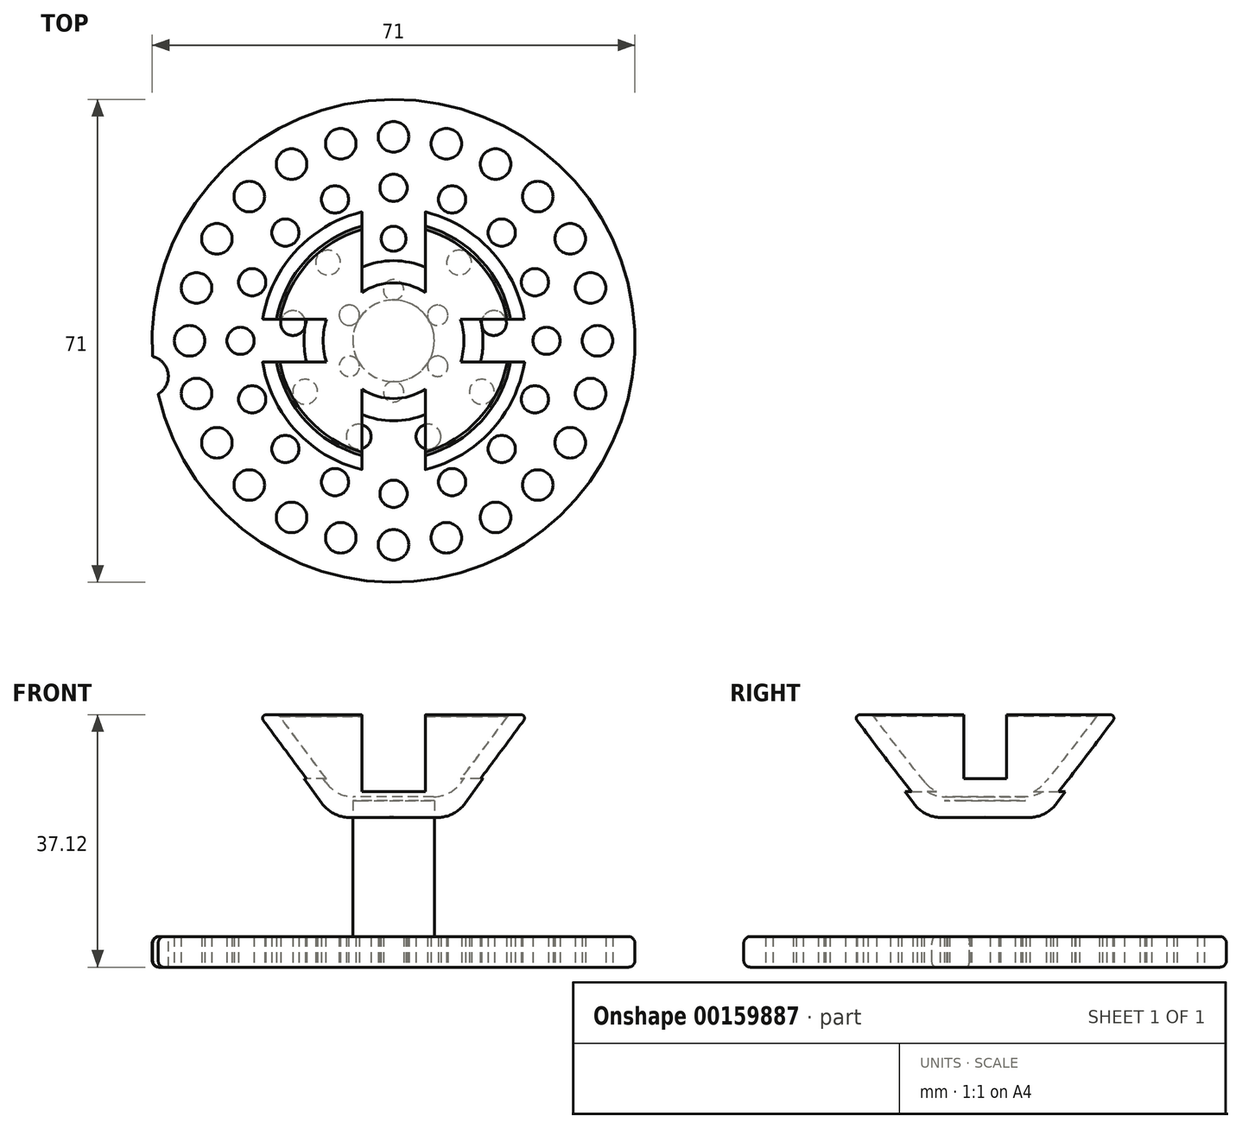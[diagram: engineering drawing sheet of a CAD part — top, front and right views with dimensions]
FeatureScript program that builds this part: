
annotation { "Feature Type Name" : "Feature", "Feature Type Description" : "" }
export const myFeature = defineFeature(function(context is Context, id is Id, definition is map)
    precondition{}
    {
        {
            var Q0;
            Q0=qCreatedBy(makeId("Top.planeOp"),FACE);
            var sketch = newSketch(context, id + "F0", { "sketchPlane" : qUnion([Q0])});
            skCircle(sketch, "E0", {"center": v(0, 0) * mm, "radius": 35.5 * mm});
            skSolve(sketch);
        }
        {
            var Q0;
            Q0=makeQuery(id+"F0.imprint","IMPRINT",FACE,{"disambiguationData":[TD([[makeQuery(id+"F0.imprint","IMPRINT",EDGE,{"derivedFrom":sQuery(id+"F0.wireOp",EDGE,"E0")}),1.0]])]});
            var sketch = newSketch(context, id + "F1", { "sketchPlane" : qUnion([Q0])});
            skCircle(sketch, "E1", {"center": v(0, 0) * mm, "radius": 7.5 * mm, "construction": true});
            skCircle(sketch, "E2", {"center": v(0, 7.5) * mm, "radius": 1.5 * mm});
            skCircle(sketch, "E3.1.1", {"center": v(-6.5, 3.75) * mm, "radius": 1.5 * mm});
            skCircle(sketch, "E3.2.1", {"center": v(-6.5, -3.75) * mm, "radius": 1.5 * mm});
            skCircle(sketch, "E3.3.1", {"center": v(0, -7.5) * mm, "radius": 1.5 * mm});
            skCircle(sketch, "E3.4.1", {"center": v(6.5, -3.75) * mm, "radius": 1.5 * mm});
            skCircle(sketch, "E3.5.1", {"center": v(6.5, 3.75) * mm, "radius": 1.5 * mm});
            skSolve(sketch);
        }
        {
            var Q0;
            Q0=makeQuery(id+"F0.imprint","IMPRINT",FACE,{"disambiguationData":[TD([[makeQuery(id+"F0.imprint","IMPRINT",EDGE,{"derivedFrom":sQuery(id+"F0.wireOp",EDGE,"E0")}),1.0]])]});
            var sketch = newSketch(context, id + "F2", { "sketchPlane" : qUnion([Q0])});
            skCircle(sketch, "E4", {"center": v(0, 0) * mm, "radius": 15 * mm, "construction": true});
            skCircle(sketch, "E5", {"center": v(0, 15) * mm, "radius": 1.83 * mm});
            skCircle(sketch, "E6.1.0", {"center": v(-9.64, 11.5) * mm, "radius": 1.83 * mm});
            skCircle(sketch, "E6.2.0", {"center": v(-14.77, 2.6) * mm, "radius": 1.83 * mm});
            skCircle(sketch, "E6.3.0", {"center": v(-13, -7.5) * mm, "radius": 1.83 * mm});
            skCircle(sketch, "E6.4.0", {"center": v(-5.13, -14.1) * mm, "radius": 1.83 * mm});
            skCircle(sketch, "E6.5.0", {"center": v(5.13, -14.1) * mm, "radius": 1.83 * mm});
            skCircle(sketch, "E6.6.0", {"center": v(13, -7.5) * mm, "radius": 1.83 * mm});
            skCircle(sketch, "E6.7.0", {"center": v(14.77, 2.6) * mm, "radius": 1.83 * mm});
            skCircle(sketch, "E6.8.0", {"center": v(9.64, 11.5) * mm, "radius": 1.83 * mm});
            skSolve(sketch);
        }
        {
            var Q0;
            Q0=makeQuery(id+"F0.imprint","IMPRINT",FACE,{"disambiguationData":[TD([[makeQuery(id+"F0.imprint","IMPRINT",EDGE,{"derivedFrom":sQuery(id+"F0.wireOp",EDGE,"E0")}),1.0]])]});
            var sketch = newSketch(context, id + "F3", { "sketchPlane" : qUnion([Q0])});
            skCircle(sketch, "E7", {"center": v(0, 0) * mm, "radius": 22.5 * mm, "construction": true});
            skCircle(sketch, "E8", {"center": v(0, 22.5) * mm, "radius": 2 * mm});
            skCircle(sketch, "E9.1.0", {"center": v(-8.61, 20.79) * mm, "radius": 2 * mm});
            skCircle(sketch, "E9.2.0", {"center": v(-15.9, 15.9) * mm, "radius": 2 * mm});
            skCircle(sketch, "E9.3.0", {"center": v(-20.79, 8.61) * mm, "radius": 2 * mm});
            skCircle(sketch, "E9.4.0", {"center": v(-22.5, 0) * mm, "radius": 2 * mm});
            skCircle(sketch, "E9.5.0", {"center": v(-20.79, -8.61) * mm, "radius": 2 * mm});
            skCircle(sketch, "E9.6.0", {"center": v(-15.9, -15.9) * mm, "radius": 2 * mm});
            skCircle(sketch, "E9.7.0", {"center": v(-8.61, -20.79) * mm, "radius": 2 * mm});
            skCircle(sketch, "E9.8.0", {"center": v(0, -22.5) * mm, "radius": 2 * mm});
            skCircle(sketch, "E9.9.0", {"center": v(8.61, -20.79) * mm, "radius": 2 * mm});
            skCircle(sketch, "E9.10.0", {"center": v(15.9, -15.9) * mm, "radius": 2 * mm});
            skCircle(sketch, "E9.11.0", {"center": v(20.79, -8.61) * mm, "radius": 2 * mm});
            skCircle(sketch, "E9.12.0", {"center": v(22.5, 0) * mm, "radius": 2 * mm});
            skCircle(sketch, "E9.13.0", {"center": v(20.79, 8.61) * mm, "radius": 2 * mm});
            skCircle(sketch, "E9.14.0", {"center": v(15.9, 15.9) * mm, "radius": 2 * mm});
            skCircle(sketch, "E9.15.0", {"center": v(8.61, 20.79) * mm, "radius": 2 * mm});
            skSolve(sketch);
        }
        {
            var Q0;
            Q0=makeQuery(id+"F0.imprint","IMPRINT",FACE,{"disambiguationData":[TD([[makeQuery(id+"F0.imprint","IMPRINT",EDGE,{"derivedFrom":sQuery(id+"F0.wireOp",EDGE,"E0")}),1.0]])]});
            var sketch = newSketch(context, id + "F4", { "sketchPlane" : qUnion([Q0])});
            skCircle(sketch, "E10", {"center": v(0, 0) * mm, "radius": 30 * mm, "construction": true});
            skCircle(sketch, "E11", {"center": v(0, 30) * mm, "radius": 2.25 * mm});
            skCircle(sketch, "E12.1.0", {"center": v(-7.76, 28.98) * mm, "radius": 2.25 * mm});
            skCircle(sketch, "E12.2.0", {"center": v(-15, 25.98) * mm, "radius": 2.25 * mm});
            skCircle(sketch, "E13.1.3.0", {"center": v(-21.21, 21.21) * mm, "radius": 2.25 * mm});
            skCircle(sketch, "E13.1.4.0", {"center": v(-25.98, 15) * mm, "radius": 2.25 * mm});
            skCircle(sketch, "E13.1.5.0", {"center": v(-28.98, 7.76) * mm, "radius": 2.25 * mm});
            skCircle(sketch, "E13.1.6.0", {"center": v(-30, 0) * mm, "radius": 2.25 * mm});
            skCircle(sketch, "E13.1.7.0", {"center": v(-28.98, -7.76) * mm, "radius": 2.25 * mm});
            skCircle(sketch, "E13.1.8.0", {"center": v(-25.98, -15) * mm, "radius": 2.25 * mm});
            skCircle(sketch, "E13.1.9.0", {"center": v(-21.21, -21.21) * mm, "radius": 2.25 * mm});
            skCircle(sketch, "E13.1.10.0", {"center": v(-15, -25.98) * mm, "radius": 2.25 * mm});
            skCircle(sketch, "E13.1.11.0", {"center": v(-7.76, -28.98) * mm, "radius": 2.25 * mm});
            skCircle(sketch, "E13.1.12.0", {"center": v(0, -30) * mm, "radius": 2.25 * mm});
            skCircle(sketch, "E13.1.13.0", {"center": v(7.76, -28.98) * mm, "radius": 2.25 * mm});
            skCircle(sketch, "E13.1.14.0", {"center": v(15, -25.98) * mm, "radius": 2.25 * mm});
            skCircle(sketch, "E13.1.15.0", {"center": v(21.21, -21.21) * mm, "radius": 2.25 * mm});
            skCircle(sketch, "E13.1.16.0", {"center": v(25.98, -15) * mm, "radius": 2.25 * mm});
            skCircle(sketch, "E13.1.17.0", {"center": v(28.98, -7.76) * mm, "radius": 2.25 * mm});
            skCircle(sketch, "E13.1.18.0", {"center": v(30, 0) * mm, "radius": 2.25 * mm});
            skCircle(sketch, "E13.1.19.0", {"center": v(28.98, 7.76) * mm, "radius": 2.25 * mm});
            skCircle(sketch, "E13.1.20.0", {"center": v(25.98, 15) * mm, "radius": 2.25 * mm});
            skCircle(sketch, "E13.1.21.0", {"center": v(21.21, 21.21) * mm, "radius": 2.25 * mm});
            skCircle(sketch, "E13.1.22.0", {"center": v(15, 25.98) * mm, "radius": 2.25 * mm});
            skCircle(sketch, "E13.1.23.0", {"center": v(7.76, 28.98) * mm, "radius": 2.25 * mm});
            skSolve(sketch);
        }
        {
            var Q0;
            Q0=qSketchRegion(id+"F4",true);
            extrude(context, id + "F5", {"entities" : qUnion([Q0]), "depth" : 5 * mm});
        }
        {
            var Q0;
            Q0=qSketchRegion(id+"F3",true);
            extrude(context, id + "F6", {"entities" : qUnion([Q0]), "depth" : 5 * mm});
        }
        {
            var Q0;
            Q0=qSketchRegion(id+"F2",true);
            extrude(context, id + "F7", {"entities" : qUnion([Q0]), "depth" : 5 * mm});
        }
        {
            var Q0;
            Q0=qSketchRegion(id+"F1",true);
            extrude(context, id + "F8", {"entities" : qUnion([Q0]), "depth" : 5 * mm});
        }
        {
            var Q0;
            Q0=qSketchRegion(id+"F0",true);
            extrude(context, id + "F9", {"entities" : qUnion([Q0]), "depth" : 4.5 * mm});
        }
        {
            var Q0;
            Q0=makeQuery(id+"F5.opExtrude","SWEPT_BODY",BODY,{"disambiguationData":[OSD([sQuery(id+"F4.wireOp",EDGE,"E11")])]});
            var Q1;
            Q1=makeQuery(id+"F5.opExtrude","SWEPT_BODY",BODY,{"disambiguationData":[OSD([sQuery(id+"F4.wireOp",EDGE,"E13.1.3.0")])]});
            var Q2;
            Q2=makeQuery(id+"F5.opExtrude","SWEPT_BODY",BODY,{"disambiguationData":[OSD([sQuery(id+"F4.wireOp",EDGE,"E13.1.7.0")])]});
            var Q3;
            Q3=makeQuery(id+"F5.opExtrude","SWEPT_BODY",BODY,{"disambiguationData":[OSD([sQuery(id+"F4.wireOp",EDGE,"E12.1.0")])]});
            var Q4;
            Q4=makeQuery(id+"F5.opExtrude","SWEPT_BODY",BODY,{"disambiguationData":[OSD([sQuery(id+"F4.wireOp",EDGE,"E12.2.0")])]});
            var Q5;
            Q5=makeQuery(id+"F5.opExtrude","SWEPT_BODY",BODY,{"disambiguationData":[OSD([sQuery(id+"F4.wireOp",EDGE,"E13.1.4.0")])]});
            var Q6;
            Q6=makeQuery(id+"F5.opExtrude","SWEPT_BODY",BODY,{"disambiguationData":[OSD([sQuery(id+"F4.wireOp",EDGE,"E13.1.5.0")])]});
            var Q7;
            Q7=makeQuery(id+"F5.opExtrude","SWEPT_BODY",BODY,{"disambiguationData":[OSD([sQuery(id+"F4.wireOp",EDGE,"E13.1.6.0")])]});
            var Q8;
            Q8=makeQuery(id+"F5.opExtrude","SWEPT_BODY",BODY,{"disambiguationData":[OSD([sQuery(id+"F4.wireOp",EDGE,"E13.1.8.0")])]});
            var Q9;
            Q9=makeQuery(id+"F5.opExtrude","SWEPT_BODY",BODY,{"disambiguationData":[OSD([sQuery(id+"F4.wireOp",EDGE,"E13.1.9.0")])]});
            var Q10;
            Q10=makeQuery(id+"F5.opExtrude","SWEPT_BODY",BODY,{"disambiguationData":[OSD([sQuery(id+"F4.wireOp",EDGE,"E13.1.10.0")])]});
            var Q11;
            Q11=makeQuery(id+"F5.opExtrude","SWEPT_BODY",BODY,{"disambiguationData":[OSD([sQuery(id+"F4.wireOp",EDGE,"E13.1.11.0")])]});
            var Q12;
            Q12=makeQuery(id+"F5.opExtrude","SWEPT_BODY",BODY,{"disambiguationData":[OSD([sQuery(id+"F4.wireOp",EDGE,"E13.1.12.0")])]});
            var Q13;
            Q13=makeQuery(id+"F5.opExtrude","SWEPT_BODY",BODY,{"disambiguationData":[OSD([sQuery(id+"F4.wireOp",EDGE,"E13.1.13.0")])]});
            var Q14;
            Q14=makeQuery(id+"F5.opExtrude","SWEPT_BODY",BODY,{"disambiguationData":[OSD([sQuery(id+"F4.wireOp",EDGE,"E13.1.14.0")])]});
            var Q15;
            Q15=makeQuery(id+"F5.opExtrude","SWEPT_BODY",BODY,{"disambiguationData":[OSD([sQuery(id+"F4.wireOp",EDGE,"E13.1.15.0")])]});
            var Q16;
            Q16=makeQuery(id+"F5.opExtrude","SWEPT_BODY",BODY,{"disambiguationData":[OSD([sQuery(id+"F4.wireOp",EDGE,"E13.1.16.0")])]});
            var Q17;
            Q17=makeQuery(id+"F5.opExtrude","SWEPT_BODY",BODY,{"disambiguationData":[OSD([sQuery(id+"F4.wireOp",EDGE,"E13.1.17.0")])]});
            var Q18;
            Q18=makeQuery(id+"F5.opExtrude","SWEPT_BODY",BODY,{"disambiguationData":[OSD([sQuery(id+"F4.wireOp",EDGE,"E13.1.18.0")])]});
            var Q19;
            Q19=makeQuery(id+"F5.opExtrude","SWEPT_BODY",BODY,{"disambiguationData":[OSD([sQuery(id+"F4.wireOp",EDGE,"E13.1.19.0")])]});
            var Q20;
            Q20=makeQuery(id+"F5.opExtrude","SWEPT_BODY",BODY,{"disambiguationData":[OSD([sQuery(id+"F4.wireOp",EDGE,"E13.1.20.0")])]});
            var Q21;
            Q21=makeQuery(id+"F5.opExtrude","SWEPT_BODY",BODY,{"disambiguationData":[OSD([sQuery(id+"F4.wireOp",EDGE,"E13.1.21.0")])]});
            var Q22;
            Q22=makeQuery(id+"F5.opExtrude","SWEPT_BODY",BODY,{"disambiguationData":[OSD([sQuery(id+"F4.wireOp",EDGE,"E13.1.22.0")])]});
            var Q23;
            Q23=makeQuery(id+"F5.opExtrude","SWEPT_BODY",BODY,{"disambiguationData":[OSD([sQuery(id+"F4.wireOp",EDGE,"E13.1.23.0")])]});
            var Q24;
            Q24=makeQuery(id+"F6.opExtrude","SWEPT_BODY",BODY,{"disambiguationData":[OSD([sQuery(id+"F3.wireOp",EDGE,"E9.15.0")])]});
            var Q25;
            Q25=makeQuery(id+"F6.opExtrude","SWEPT_BODY",BODY,{"disambiguationData":[OSD([sQuery(id+"F3.wireOp",EDGE,"E8")])]});
            var Q26;
            Q26=makeQuery(id+"F6.opExtrude","SWEPT_BODY",BODY,{"disambiguationData":[OSD([sQuery(id+"F3.wireOp",EDGE,"E9.1.0")])]});
            var Q27;
            Q27=makeQuery(id+"F6.opExtrude","SWEPT_BODY",BODY,{"disambiguationData":[OSD([sQuery(id+"F3.wireOp",EDGE,"E9.2.0")])]});
            var Q28;
            Q28=makeQuery(id+"F6.opExtrude","SWEPT_BODY",BODY,{"disambiguationData":[OSD([sQuery(id+"F3.wireOp",EDGE,"E9.3.0")])]});
            var Q29;
            Q29=makeQuery(id+"F6.opExtrude","SWEPT_BODY",BODY,{"disambiguationData":[OSD([sQuery(id+"F3.wireOp",EDGE,"E9.4.0")])]});
            var Q30;
            Q30=makeQuery(id+"F6.opExtrude","SWEPT_BODY",BODY,{"disambiguationData":[OSD([sQuery(id+"F3.wireOp",EDGE,"E9.5.0")])]});
            var Q31;
            Q31=makeQuery(id+"F6.opExtrude","SWEPT_BODY",BODY,{"disambiguationData":[OSD([sQuery(id+"F3.wireOp",EDGE,"E9.6.0")])]});
            var Q32;
            Q32=makeQuery(id+"F6.opExtrude","SWEPT_BODY",BODY,{"disambiguationData":[OSD([sQuery(id+"F3.wireOp",EDGE,"E9.7.0")])]});
            var Q33;
            Q33=makeQuery(id+"F6.opExtrude","SWEPT_BODY",BODY,{"disambiguationData":[OSD([sQuery(id+"F3.wireOp",EDGE,"E9.8.0")])]});
            var Q34;
            Q34=makeQuery(id+"F6.opExtrude","SWEPT_BODY",BODY,{"disambiguationData":[OSD([sQuery(id+"F3.wireOp",EDGE,"E9.9.0")])]});
            var Q35;
            Q35=makeQuery(id+"F6.opExtrude","SWEPT_BODY",BODY,{"disambiguationData":[OSD([sQuery(id+"F3.wireOp",EDGE,"E9.10.0")])]});
            var Q36;
            Q36=makeQuery(id+"F6.opExtrude","SWEPT_BODY",BODY,{"disambiguationData":[OSD([sQuery(id+"F3.wireOp",EDGE,"E9.11.0")])]});
            var Q37;
            Q37=makeQuery(id+"F6.opExtrude","SWEPT_BODY",BODY,{"disambiguationData":[OSD([sQuery(id+"F3.wireOp",EDGE,"E9.12.0")])]});
            var Q38;
            Q38=makeQuery(id+"F6.opExtrude","SWEPT_BODY",BODY,{"disambiguationData":[OSD([sQuery(id+"F3.wireOp",EDGE,"E9.13.0")])]});
            var Q39;
            Q39=makeQuery(id+"F6.opExtrude","SWEPT_BODY",BODY,{"disambiguationData":[OSD([sQuery(id+"F3.wireOp",EDGE,"E9.14.0")])]});
            var Q40;
            Q40=makeQuery(id+"F7.opExtrude","SWEPT_BODY",BODY,{"disambiguationData":[OSD([sQuery(id+"F2.wireOp",EDGE,"E6.8.0")])]});
            var Q41;
            Q41=makeQuery(id+"F7.opExtrude","SWEPT_BODY",BODY,{"disambiguationData":[OSD([sQuery(id+"F2.wireOp",EDGE,"E6.7.0")])]});
            var Q42;
            Q42=makeQuery(id+"F7.opExtrude","SWEPT_BODY",BODY,{"disambiguationData":[OSD([sQuery(id+"F2.wireOp",EDGE,"E6.6.0")])]});
            var Q43;
            Q43=makeQuery(id+"F7.opExtrude","SWEPT_BODY",BODY,{"disambiguationData":[OSD([sQuery(id+"F2.wireOp",EDGE,"E6.5.0")])]});
            var Q44;
            Q44=makeQuery(id+"F7.opExtrude","SWEPT_BODY",BODY,{"disambiguationData":[OSD([sQuery(id+"F2.wireOp",EDGE,"E6.4.0")])]});
            var Q45;
            Q45=makeQuery(id+"F7.opExtrude","SWEPT_BODY",BODY,{"disambiguationData":[OSD([sQuery(id+"F2.wireOp",EDGE,"E6.3.0")])]});
            var Q46;
            Q46=makeQuery(id+"F7.opExtrude","SWEPT_BODY",BODY,{"disambiguationData":[OSD([sQuery(id+"F2.wireOp",EDGE,"E6.2.0")])]});
            var Q47;
            Q47=makeQuery(id+"F7.opExtrude","SWEPT_BODY",BODY,{"disambiguationData":[OSD([sQuery(id+"F2.wireOp",EDGE,"E6.1.0")])]});
            var Q48;
            Q48=makeQuery(id+"F7.opExtrude","SWEPT_BODY",BODY,{"disambiguationData":[OSD([sQuery(id+"F2.wireOp",EDGE,"E5")])]});
            var Q49;
            Q49=makeQuery(id+"F8.opExtrude","SWEPT_BODY",BODY,{"disambiguationData":[OSD([sQuery(id+"F1.wireOp",EDGE,"E2")])]});
            var Q50;
            Q50=makeQuery(id+"F8.opExtrude","SWEPT_BODY",BODY,{"disambiguationData":[OSD([sQuery(id+"F1.wireOp",EDGE,"E3.5.1")])]});
            var Q51;
            Q51=makeQuery(id+"F8.opExtrude","SWEPT_BODY",BODY,{"disambiguationData":[OSD([sQuery(id+"F1.wireOp",EDGE,"E3.4.1")])]});
            var Q52;
            Q52=makeQuery(id+"F8.opExtrude","SWEPT_BODY",BODY,{"disambiguationData":[OSD([sQuery(id+"F1.wireOp",EDGE,"E3.3.1")])]});
            var Q53;
            Q53=makeQuery(id+"F8.opExtrude","SWEPT_BODY",BODY,{"disambiguationData":[OSD([sQuery(id+"F1.wireOp",EDGE,"E3.2.1")])]});
            var Q54;
            Q54=makeQuery(id+"F8.opExtrude","SWEPT_BODY",BODY,{"disambiguationData":[OSD([sQuery(id+"F1.wireOp",EDGE,"E3.1.1")])]});
            var Q55;
            Q55=makeQuery(id+"F9.opExtrude","SWEPT_BODY",BODY,{"disambiguationData":[OSD([sQuery(id+"F0.wireOp",EDGE,"E0")])]});
            booleanBodies(context, id + "F10", {"operationType" : BooleanOperationType.SUBTRACTION, "tools" : qUnion([Q0, Q1, Q2, Q3, Q4, Q5, Q6, Q7, Q8, Q9, Q10, Q11, Q12, Q13, Q14, Q15, Q16, Q17, Q18, Q19, Q20, Q21, Q22, Q23, Q24, Q25, Q26, Q27, Q28, Q29, Q30, Q31, Q32, Q33, Q34, Q35, Q36, Q37, Q38, Q39, Q40, Q41, Q42, Q43, Q44, Q45, Q46, Q47, Q48, Q49, Q50, Q51, Q52, Q53, Q54]), "targets" : qUnion([Q55])});
        }
        {
            var Q0;
            Q0=makeQuery(id+"F9.opExtrude","CAP_EDGE",EDGE,{"disambiguationData":[OSD([sQuery(id+"F0.wireOp",EDGE,"E0")])],"isStart":true});
            var Q1;
            Q1=makeQuery(id+"F9.opExtrude","CAP_EDGE",EDGE,{"disambiguationData":[OSD([sQuery(id+"F0.wireOp",EDGE,"E0")])],"isStart":false});
            fillet(context, id + "F11", {"entities" : qUnion([Q0, Q1]), "radius" : 1 * mm, "tangentPropagation" : true, "allowEdgeOverflow" : false});
        }
        {
            var Q0;
            Q0=makeQuery(id+"F9.opExtrude","CAP_FACE",FACE,{"disambiguationData":[OSD([sQuery(id+"F0.wireOp",EDGE,"E0")])],"isStart":false});
            var sketch = newSketch(context, id + "F12", { "sketchPlane" : qUnion([Q0])});
            skCircle(sketch, "E14", {"center": v(0, 0) * mm, "radius": 6 * mm});
            skSolve(sketch);
        }
        {
            var Q0;
            Q0=makeQuery(id+"F12.imprint","IMPRINT",FACE,{"disambiguationData":[TD([[makeQuery(id+"F12.imprint","IMPRINT",EDGE,{"derivedFrom":sQuery(id+"F12.wireOp",EDGE,"E14")}),1.0]])]});
            extrude(context, id + "F13", {"entities" : qUnion([Q0]), "operationType" : NewBodyOperationType.ADD, "depth" : 20 * mm, "offsetDistance" : 25 * mm});
        }
        {
            var Q0;
            Q0=makeQuery(id+"F9.opExtrude","CAP_FACE",FACE,{"disambiguationData":[OSD([sQuery(id+"F0.wireOp",EDGE,"E0")])],"isStart":false});
            var sketch = newSketch(context, id + "F14", { "sketchPlane" : qUnion([Q0])});
            skCircle(sketch, "E15", {"center": v(0, 0) * mm, "radius": 36.5 * mm, "construction": true});
            skCircle(sketch, "E16", {"center": v(-36.12, -5.23) * mm, "radius": 3 * mm});
            skSolve(sketch);
        }
        {
            var Q0;
            Q0=makeQuery(id+"F14.imprint","IMPRINT",FACE,{"disambiguationData":[TD([[makeQuery(id+"F14.imprint","IMPRINT",EDGE,{"derivedFrom":sQuery(id+"F14.wireOp",EDGE,"E16")}),1.0]])]});
            extrude(context, id + "F15", {"entities" : qUnion([Q0]), "operationType" : NewBodyOperationType.REMOVE, "oppositeDirection" : true, "depth" : 25 * mm});
        }
        {
            var Q0;
            Q0=qCreatedBy(makeId("Front.planeOp"),FACE);
            var sketch = newSketch(context, id + "F16", { "sketchPlane" : qUnion([Q0])});
            skLineSegment(sketch, "E17", {"start": v(0, 64.6) * mm, "end": v(0, 86.12) * mm, "construction": true});
            skLineSegment(sketch, "E18", {"start": v(-20, 85.12) * mm, "end": v(-9, 69.99) * mm});
            skLineSegment(sketch, "E19", {"start": v(0, 70.12) * mm, "end": v(0, 86.12) * mm});
            skLineSegment(sketch, "E20", {"start": v(-20, 85.12) * mm, "end": v(-17.2, 85.12) * mm});
            skLineSegment(sketch, "E21", {"start": v(-17.2, 85.12) * mm, "end": v(-8.44, 73.07) * mm});
            skLineSegment(sketch, "E22", {"start": v(-8.44, 73.07) * mm, "end": v(0, 73.07) * mm});
            skLineSegment(sketch, "E23", {"start": v(-9, 69.99) * mm, "end": v(0, 70.12) * mm});
            skSolve(sketch);
        }
        {
            var Q0;
            Q0=makeQuery(id+"F16.imprint","IMPRINT",FACE,{"disambiguationData":[TD([[makeQuery(id+"F16.imprint","IMPRINT",EDGE,{"derivedFrom":sQuery(id+"F16.wireOp",EDGE,"E18")}),1.0]])]});
            var Q1;
            Q1=sQuery(id+"F16.wireOp",EDGE,"E19");
            revolve(context, id + "F17", {"operationType" : NewBodyOperationType.ADD, "surfaceOperationType" : NewSurfaceOperationType.NEW, "entities" : qUnion([Q0]), "axis" : qUnion([Q1]), "revolveType" : RevolveType.FULL});
        }
        {
            var Q0;
            Q0=makeQuery(id+"F17.opRevolve","SWEPT_BODY",BODY,{"disambiguationData":[OSD([sQuery(id+"F16.wireOp",EDGE,"E18"),sQuery(id+"F16.wireOp",EDGE,"ekqP7qBP-ulQC-kSXt-n5Og-ePe3p9eNB1yX"),sQuery(id+"F16.wireOp",EDGE,"E19"),sQuery(id+"F16.wireOp",EDGE,"E20"),sQuery(id+"F16.wireOp",EDGE,"E21"),sQuery(id+"F16.wireOp",EDGE,"E22")])]});
            transform(context, id + "F18", {"entities" : qUnion([Q0]), "transformType" : TransformType.TRANSLATION_3D, "dx" : 0 * mm, "dy" : 0 * mm, "dz" : -48 * mm, "makeCopy" : false});
        }
        {
            var Q0;
            Q0=qCreatedBy(makeId("Front.planeOp"),FACE);
            var sketch = newSketch(context, id + "F19", { "sketchPlane" : qUnion([Q0])});
            skLineSegment(sketch, "E24.bottom", {"start": v(4.66, 25.8) * mm, "end": v(-4.66, 25.8) * mm});
            skLineSegment(sketch, "E24.top", {"start": v(4.66, 51.49) * mm, "end": v(-4.66, 51.49) * mm});
            skLineSegment(sketch, "E24.left", {"start": v(4.66, 25.8) * mm, "end": v(4.66, 51.49) * mm});
            skLineSegment(sketch, "E24.right", {"start": v(-4.66, 25.8) * mm, "end": v(-4.66, 51.49) * mm});
            skPoint(sketch, "E24.middle", {"position": v(0, 38.65) * mm});
            skLineSegment(sketch, "E25", {"start": v(0, 59.77) * mm, "end": v(0, 0) * mm, "construction": true});
            skSolve(sketch);
        }
        {
            var Q0;
            Q0 = qSketchRegion(id + "F19", true);
            extrude(context, id + "F20", {"entities" : qUnion([Q0]), "endBound" : BoundingType.SYMMETRIC, "depth" : 45 * mm, "offsetDistance" : 25 * mm});
        }
        {
            var Q0;
            {var subQ0=sQuery(id+"F16.wireOp",EDGE,"E20");var subQ1=sQuery(id+"F16.wireOp",EDGE,"E21");Q0=makeQuery(id+"F24O2oq0PfPqQpG_3.opBoolean","SPLIT",EDGE,{"disambiguationData":[TD([makeQuery(id+"FJ4bphDz8gUAr4i_3.opPattern","COPY",FACE,{"derivedFrom":makeQuery(id+"F20.opExtrude","SWEPT_FACE",FACE,{"disambiguationData":[OSD([sQuery(id+"F19.wireOp",EDGE,"E24.left")])]}),"instanceName":"2"})])],"derivedFrom":makeQuery(id+"F17.opRevolve","SWEPT_EDGE",EDGE,{"disambiguationData":[OSD([subQ0,subQ1])]})});}
            var Q1;
            {var subQ0=sQuery(id+"F16.wireOp",EDGE,"E20");var subQ1=sQuery(id+"F16.wireOp",EDGE,"E21");Q1=makeQuery(id+"F24O2oq0PfPqQpG_3.opBoolean","SPLIT",EDGE,{"disambiguationData":[TD([makeQuery(id+"FJ4bphDz8gUAr4i_3.opPattern","COPY",FACE,{"derivedFrom":makeQuery(id+"F20.opExtrude","SWEPT_FACE",FACE,{"disambiguationData":[OSD([sQuery(id+"F19.wireOp",EDGE,"E24.left")])]}),"instanceName":"1"})])],"derivedFrom":makeQuery(id+"F17.opRevolve","SWEPT_EDGE",EDGE,{"disambiguationData":[OSD([subQ0,subQ1])]})});}
            var Q2;
            {var subQ0=sQuery(id+"F16.wireOp",EDGE,"E20");var subQ1=sQuery(id+"F16.wireOp",EDGE,"E21");Q2=makeQuery(id+"F24O2oq0PfPqQpG_3.opBoolean","SPLIT",EDGE,{"disambiguationData":[TD([makeQuery(id+"F20.opExtrude","SWEPT_FACE",FACE,{"disambiguationData":[OSD([sQuery(id+"F19.wireOp",EDGE,"E24.left")])]})])],"derivedFrom":makeQuery(id+"F17.opRevolve","SWEPT_EDGE",EDGE,{"disambiguationData":[OSD([subQ0,subQ1])]})});}
            var Q3;
            {var subQ0=sQuery(id+"F16.wireOp",EDGE,"E20");var subQ1=sQuery(id+"F16.wireOp",EDGE,"E21");Q3=makeQuery(id+"F24O2oq0PfPqQpG_3.opBoolean","SPLIT",EDGE,{"disambiguationData":[TD([makeQuery(id+"F20.opExtrude","SWEPT_FACE",FACE,{"disambiguationData":[OSD([sQuery(id+"F19.wireOp",EDGE,"E24.right")])]})])],"derivedFrom":makeQuery(id+"F17.opRevolve","SWEPT_EDGE",EDGE,{"disambiguationData":[OSD([subQ0,subQ1])]})});}
            var Q4;
            {var subQ0=sQuery(id+"F16.wireOp",EDGE,"E20");var subQ1=sQuery(id+"F16.wireOp",EDGE,"E21");Q4=makeQuery(id+"F24O2oq0PfPqQpG_3.opBoolean","SPLIT",EDGE,{"disambiguationData":[TD([makeQuery(id+"FJ4bphDz8gUAr4i_3.opPattern","COPY",FACE,{"derivedFrom":makeQuery(id+"F20.opExtrude","SWEPT_FACE",FACE,{"disambiguationData":[OSD([sQuery(id+"F19.wireOp",EDGE,"E24.left")])]}),"instanceName":"4"})])],"derivedFrom":makeQuery(id+"F17.opRevolve","SWEPT_EDGE",EDGE,{"disambiguationData":[OSD([subQ0,subQ1])]})});}
            var Q5;
            {var subQ0=sQuery(id+"F16.wireOp",EDGE,"E20");var subQ1=sQuery(id+"F16.wireOp",EDGE,"E21");Q5=makeQuery(id+"F24O2oq0PfPqQpG_3.opBoolean","SPLIT",EDGE,{"disambiguationData":[TD([makeQuery(id+"FJ4bphDz8gUAr4i_3.opPattern","COPY",FACE,{"derivedFrom":makeQuery(id+"F20.opExtrude","SWEPT_FACE",FACE,{"disambiguationData":[OSD([sQuery(id+"F19.wireOp",EDGE,"E24.left")])]}),"instanceName":"3"})])],"derivedFrom":makeQuery(id+"F17.opRevolve","SWEPT_EDGE",EDGE,{"disambiguationData":[OSD([subQ0,subQ1])]})});}
            chamfer(context, id + "F21", {"entities" : qUnion([Q0, Q1, Q2, Q3, Q4, Q5]), "width" : 0.6 * mm, "tangentPropagation" : true});
        }
        {
            var Q0;
            {var subQ0=sQuery(id+"F16.wireOp",EDGE,"E18");var subQ1=sQuery(id+"F16.wireOp",EDGE,"E20");Q0=makeQuery(id+"F24O2oq0PfPqQpG_3.opBoolean","SPLIT",EDGE,{"disambiguationData":[TD([makeQuery(id+"FJ4bphDz8gUAr4i_3.opPattern","COPY",FACE,{"derivedFrom":makeQuery(id+"F20.opExtrude","SWEPT_FACE",FACE,{"disambiguationData":[OSD([sQuery(id+"F19.wireOp",EDGE,"E24.left")])]}),"instanceName":"2"})])],"derivedFrom":makeQuery(id+"F17.opRevolve","SWEPT_EDGE",EDGE,{"disambiguationData":[OSD([subQ0,subQ1])]})});}
            var Q1;
            {var subQ0=sQuery(id+"F16.wireOp",EDGE,"E18");var subQ1=sQuery(id+"F16.wireOp",EDGE,"E20");Q1=makeQuery(id+"F24O2oq0PfPqQpG_3.opBoolean","SPLIT",EDGE,{"disambiguationData":[TD([makeQuery(id+"FJ4bphDz8gUAr4i_3.opPattern","COPY",FACE,{"derivedFrom":makeQuery(id+"F20.opExtrude","SWEPT_FACE",FACE,{"disambiguationData":[OSD([sQuery(id+"F19.wireOp",EDGE,"E24.left")])]}),"instanceName":"1"})])],"derivedFrom":makeQuery(id+"F17.opRevolve","SWEPT_EDGE",EDGE,{"disambiguationData":[OSD([subQ0,subQ1])]})});}
            var Q2;
            {var subQ0=sQuery(id+"F16.wireOp",EDGE,"E18");var subQ1=sQuery(id+"F16.wireOp",EDGE,"E20");Q2=makeQuery(id+"F24O2oq0PfPqQpG_3.opBoolean","SPLIT",EDGE,{"disambiguationData":[TD([makeQuery(id+"F20.opExtrude","SWEPT_FACE",FACE,{"disambiguationData":[OSD([sQuery(id+"F19.wireOp",EDGE,"E24.left")])]})])],"derivedFrom":makeQuery(id+"F17.opRevolve","SWEPT_EDGE",EDGE,{"disambiguationData":[OSD([subQ0,subQ1])]})});}
            var Q3;
            {var subQ0=sQuery(id+"F16.wireOp",EDGE,"E18");var subQ1=sQuery(id+"F16.wireOp",EDGE,"E20");Q3=makeQuery(id+"F24O2oq0PfPqQpG_3.opBoolean","SPLIT",EDGE,{"disambiguationData":[TD([makeQuery(id+"F20.opExtrude","SWEPT_FACE",FACE,{"disambiguationData":[OSD([sQuery(id+"F19.wireOp",EDGE,"E24.right")])]})])],"derivedFrom":makeQuery(id+"F17.opRevolve","SWEPT_EDGE",EDGE,{"disambiguationData":[OSD([subQ0,subQ1])]})});}
            var Q4;
            {var subQ0=sQuery(id+"F16.wireOp",EDGE,"E18");var subQ1=sQuery(id+"F16.wireOp",EDGE,"E20");Q4=makeQuery(id+"F24O2oq0PfPqQpG_3.opBoolean","SPLIT",EDGE,{"disambiguationData":[TD([makeQuery(id+"FJ4bphDz8gUAr4i_3.opPattern","COPY",FACE,{"derivedFrom":makeQuery(id+"F20.opExtrude","SWEPT_FACE",FACE,{"disambiguationData":[OSD([sQuery(id+"F19.wireOp",EDGE,"E24.left")])]}),"instanceName":"4"})])],"derivedFrom":makeQuery(id+"F17.opRevolve","SWEPT_EDGE",EDGE,{"disambiguationData":[OSD([subQ0,subQ1])]})});}
            var Q5;
            {var subQ0=sQuery(id+"F16.wireOp",EDGE,"E18");var subQ1=sQuery(id+"F16.wireOp",EDGE,"E20");Q5=makeQuery(id+"F24O2oq0PfPqQpG_3.opBoolean","SPLIT",EDGE,{"disambiguationData":[TD([makeQuery(id+"FJ4bphDz8gUAr4i_3.opPattern","COPY",FACE,{"derivedFrom":makeQuery(id+"F20.opExtrude","SWEPT_FACE",FACE,{"disambiguationData":[OSD([sQuery(id+"F19.wireOp",EDGE,"E24.left")])]}),"instanceName":"3"})])],"derivedFrom":makeQuery(id+"F17.opRevolve","SWEPT_EDGE",EDGE,{"disambiguationData":[OSD([subQ0,subQ1])]})});}
            fillet(context, id + "F22", {"entities" : qUnion([Q0, Q1, Q2, Q3, Q4, Q5]), "tangentPropagation" : true, "radius" : .5 * mm, "defaultsChanged" : false, "vertexSettings" : [], "allowEdgeOverflow" : false});
        }
        {
            var Q0;
            Q0=makeQuery(id+"F17.opRevolve","SWEPT_EDGE",EDGE,{"disambiguationData":[OSD([sQuery(id+"F16.wireOp",EDGE,"E18"),sQuery(id+"F16.wireOp",EDGE,"E23")])]});
            fillet(context, id + "F23", {"entities" : qUnion([Q0]), "tangentPropagation" : true, "radius" : 5 * mm, "defaultsChanged" : false, "vertexSettings" : [], "allowEdgeOverflow" : false});
        }
        {
            var Q0;
            Q0=makeQuery(id+"F17.opRevolve","SWEPT_EDGE",EDGE,{"disambiguationData":[OSD([sQuery(id+"F16.wireOp",EDGE,"E21"),sQuery(id+"F16.wireOp",EDGE,"E22")])]});
            fillet(context, id + "F24", {"entities" : qUnion([Q0]), "tangentPropagation" : true, "radius" : 5 * mm, "defaultsChanged" : false, "vertexSettings" : [], "allowEdgeOverflow" : false});
        }
        {
            var Q0;
            Q0=qCreatedBy(makeId("Right.planeOp"),FACE);
            var sketch = newSketch(context, id + "F25", { "sketchPlane" : qUnion([Q0])});
            skLineSegment(sketch, "E26.bottom", {"start": v(3.19, 41.64) * mm, "end": v(-3.12, 41.64) * mm});
            skLineSegment(sketch, "E26.top", {"start": v(3.19, 24.31) * mm, "end": v(-3.12, 24.31) * mm});
            skLineSegment(sketch, "E26.left", {"start": v(3.19, 41.64) * mm, "end": v(3.19, 24.31) * mm});
            skLineSegment(sketch, "E26.right", {"start": v(-3.12, 41.64) * mm, "end": v(-3.12, 24.31) * mm});
            skSolve(sketch);
        }
        {
            var Q0;
            Q0 = qSketchRegion(id + "F25", true);
            extrude(context, id + "F26", {"entities" : qUnion([Q0]), "endBound" : BoundingType.SYMMETRIC, "depth" : 45 * mm, "offsetDistance" : 25 * mm});
        }
        {
            var Q0;
            Q0=makeQuery(id+"F26.opExtrude","SWEPT_BODY",BODY,{"disambiguationData":[OSD([sQuery(id+"F25.wireOp",EDGE,"E26.bottom"),sQuery(id+"F25.wireOp",EDGE,"E26.top"),sQuery(id+"F25.wireOp",EDGE,"E26.left"),sQuery(id+"F25.wireOp",EDGE,"E26.right")])]});
            transform(context, id + "F27", {"entities" : qUnion([Q0]), "transformType" : TransformType.TRANSLATION_3D, "dx" : 0 * mm, "dy" : 0 * mm, "dz" : 3.4 * mm, "makeCopy" : false});
        }
        {
            var Q0;
            Q0=makeQuery(id+"F20.opExtrude","SWEPT_BODY",BODY,{"disambiguationData":[OSD([sQuery(id+"F19.wireOp",EDGE,"E24.bottom"),sQuery(id+"F19.wireOp",EDGE,"E24.top"),sQuery(id+"F19.wireOp",EDGE,"E24.left"),sQuery(id+"F19.wireOp",EDGE,"E24.right")])]});
            var Q1;
            Q1=makeQuery(id+"F26.opExtrude","SWEPT_BODY",BODY,{"disambiguationData":[OSD([sQuery(id+"F25.wireOp",EDGE,"E26.bottom"),sQuery(id+"F25.wireOp",EDGE,"E26.top"),sQuery(id+"F25.wireOp",EDGE,"E26.left"),sQuery(id+"F25.wireOp",EDGE,"E26.right")])]});
            var Q2;
            Q2=makeQuery(id+"F17.opRevolve","SWEPT_BODY",BODY,{"disambiguationData":[OSD([sQuery(id+"F16.wireOp",EDGE,"E18"),sQuery(id+"F16.wireOp",EDGE,"E19"),sQuery(id+"F16.wireOp",EDGE,"E20"),sQuery(id+"F16.wireOp",EDGE,"E21"),sQuery(id+"F16.wireOp",EDGE,"E22"),sQuery(id+"F16.wireOp",EDGE,"E23")])]});
            booleanBodies(context, id + "F28", {"operationType" : BooleanOperationType.SUBTRACTION, "tools" : qUnion([Q0, Q1]), "targets" : qUnion([Q2])});
        }
    });
